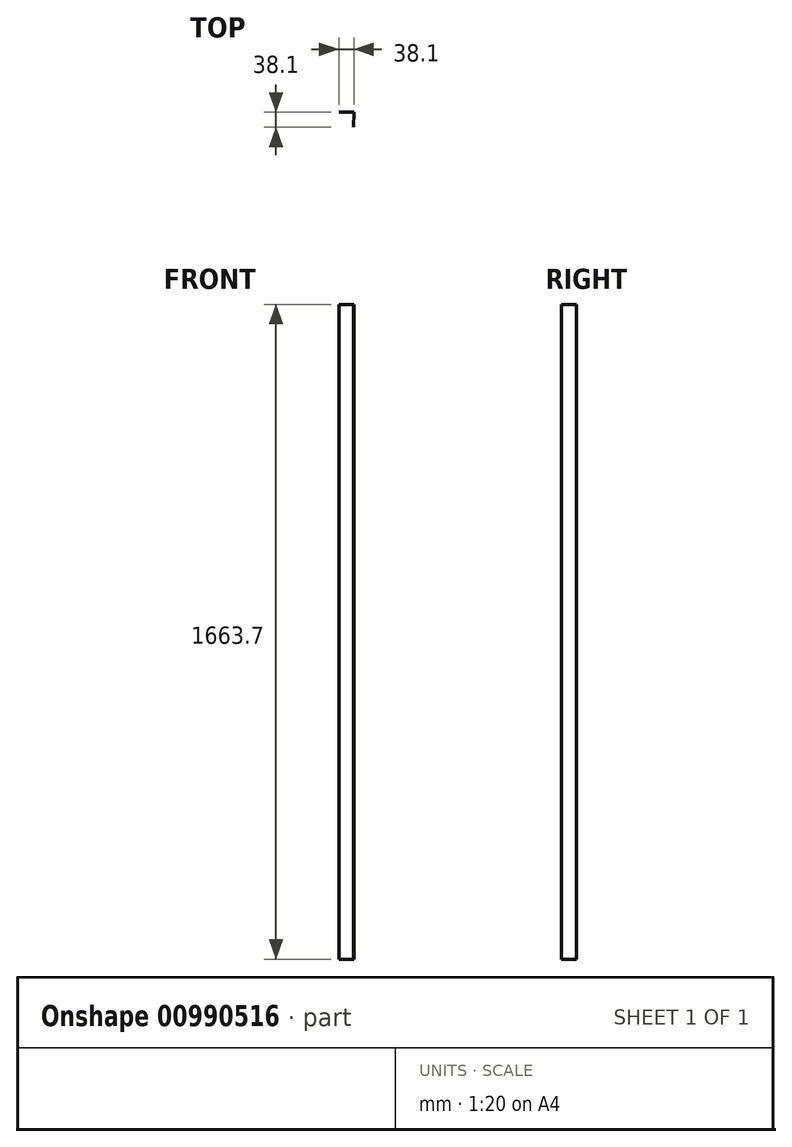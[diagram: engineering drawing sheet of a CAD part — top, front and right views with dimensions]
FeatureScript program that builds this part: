
annotation { "Feature Type Name" : "Feature", "Feature Type Description" : "" }
export const myFeature = defineFeature(function(context is Context, id is Id, definition is map)
    precondition{}
    {
        {
            var Q0;
            Q0=qCreatedBy(makeId("Top.planeOp"),FACE);
            var sketch = newSketch(context, id + "F0", { "sketchPlane" : qUnion([Q0])});
            skLineSegment(sketch, "E0", {"start": v(-171.44, 6.82) * mm, "end": v(-133.34, 6.82) * mm});
            skLineSegment(sketch, "E1", {"start": v(-133.34, 6.82) * mm, "end": v(-133.79, -31.28) * mm});
            skSolve(sketch);
        }
        {
            var Q0;
            Q0=sQuery(id+"F0.wireOp",EDGE,"E0");
            var Q1;
            Q1=sQuery(id+"F0.wireOp",EDGE,"E1");
            extrude(context, id + "F1", {"bodyType" : ToolBodyType.SURFACE, "surfaceEntities" : qUnion([Q0, Q1]), "depth" : 1663.7 * mm, "offsetDistance" : 25.4 * mm});
        }
    });
